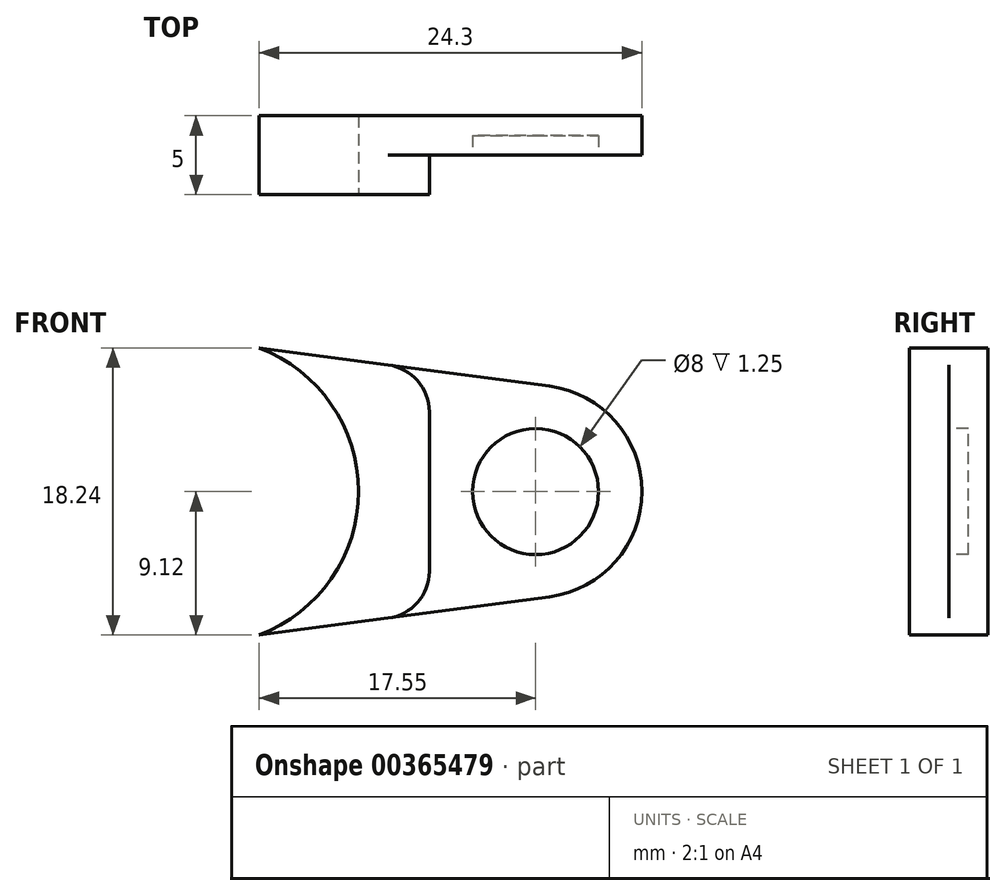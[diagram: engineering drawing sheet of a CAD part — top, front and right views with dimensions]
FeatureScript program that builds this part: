
annotation { "Feature Type Name" : "Feature", "Feature Type Description" : "" }
export const myFeature = defineFeature(function(context is Context, id is Id, definition is map)
    precondition{}
    {
        {
            var Q0;
            Q0=qCreatedBy(makeId("Front.planeOp"),FACE);
            var sketch = newSketch(context, id + "F0", { "sketchPlane" : qUnion([Q0])});
            skCircle(sketch, "E0", {"center": v(0, 0) * mm, "radius": 8 * mm});
            skCircle(sketch, "E1", {"center": v(0, 0) * mm, "radius": 9.5 * mm});
            skLineSegment(sketch, "E2", {"start": v(0, 0) * mm, "end": v(0, -1.5) * mm});
            skLineSegment(sketch, "E3", {"start": v(0, 0) * mm, "end": v(0, 1.5) * mm});
            skLineSegment(sketch, "E4", {"start": v(-32.5, 0) * mm, "end": v(-32.5, 1.5) * mm});
            skLineSegment(sketch, "E5", {"start": v(-32.5, 0) * mm, "end": v(-32.5, -1.5) * mm});
            skLineSegment(sketch, "E6", {"start": v(-32.5, -1.5) * mm, "end": v(-32.5, -2.5) * mm});
            skLineSegment(sketch, "E7", {"start": v(-23.5, -8) * mm, "end": v(-5.12, -8) * mm});
            skLineSegment(sketch, "E8.MirrorCS", {"start": v(-32.5, 1.5) * mm, "end": v(-32.5, 3.5) * mm});
            skLineSegment(sketch, "E9", {"start": v(-25.5, 0) * mm, "end": v(-25.5, -6) * mm});
            skLineSegment(sketch, "E10", {"start": v(-32.5, 1.5) * mm, "end": v(-32.5, 2.5) * mm});
            skLineSegment(sketch, "E11", {"start": v(-32.5, -1.5) * mm, "end": v(-32.5, -3.5) * mm});
            skLineSegment(sketch, "E12", {"start": v(-31.5, -3.5) * mm, "end": v(-25.5, -3.5) * mm});
            skLineSegment(sketch, "E13", {"start": v(-31.5, 3.5) * mm, "end": v(-25.5, 3.5) * mm});
            skPoint(sketch, "E14.orphan", {"position": v(-32.5, 8) * mm});
            skPoint(sketch, "E15.orphan", {"position": v(-32.5, -8) * mm});
            skPoint(sketch, "E16.visualSharp", {"position": v(-25.5, 8) * mm});
            skPoint(sketch, "E17.visualSharp", {"position": v(-25.5, -8) * mm});
            skArc(sketch, "E17.filletArc", {"start": v(-25.5, -6) * mm, "mid": v(-24.91, -7.41) * mm, "end": v(-23.5, -8) * mm});
            skPoint(sketch, "E18.visualSharp", {"position": v(-32.5, 3.5) * mm});
            skArc(sketch, "E18.filletArc", {"start": v(-31.5, 3.5) * mm, "mid": v(-32.2, 3.2) * mm, "end": v(-32.5, 2.5) * mm});
            skPoint(sketch, "E19.visualSharp", {"position": v(-32.5, -3.5) * mm});
            skArc(sketch, "E19.filletArc", {"start": v(-32.5, -2.5) * mm, "mid": v(-32.2, -3.2) * mm, "end": v(-31.5, -3.5) * mm});
            skPoint(sketch, "E20.orphan", {"position": v(-2.5, 8) * mm});
            skPoint(sketch, "E21.orphan", {"position": v(-2.5, -8) * mm});
            skLineSegment(sketch, "E22", {"start": v(-25.5, 3.5) * mm, "end": v(-8.83, 3.5) * mm});
            skLineSegment(sketch, "E23", {"start": v(-25.5, -3.5) * mm, "end": v(-25.5, 3) * mm});
            skLineSegment(sketch, "E24", {"start": v(-23.5, 5) * mm, "end": v(-8.08, 5) * mm});
            skPoint(sketch, "E25.visualSharp", {"position": v(-25.5, 5) * mm});
            skArc(sketch, "E25.filletArc", {"start": v(-23.5, 5) * mm, "mid": v(-24.91, 4.41) * mm, "end": v(-25.5, 3) * mm});
            skSolve(sketch);
        }
        {
            var Q0;
            Q0=qSketchRegion(id+"F0",true);
            extrude(context, id + "F1", {"entities" : qUnion([Q0]), "depth" : 10 * mm});
        }
        {
            var Q0;
            Q0=makeQuery(id+"F1.opExtrude","SWEPT_FACE",FACE,{"disambiguationData":[OSD([sQuery(id+"F0.wireOp",EDGE,"E4"),sQuery(id+"F0.wireOp",EDGE,"E5"),sQuery(id+"F0.wireOp",EDGE,"E10"),sQuery(id+"F0.wireOp",EDGE,"E11")])]});
            var sketch = newSketch(context, id + "F2", { "sketchPlane" : qUnion([Q0])});
            skCircle(sketch, "E26", {"center": v(5, 0) * mm, "radius": 1.5 * mm});
            skPoint(sketch, "E26.centerSnap1", {"position": v(5, -2.5) * mm});
            skSolve(sketch);
        }
        {
            var Q0;
            Q0=qSketchRegion(id+"F2",true);
            extrude(context, id + "F3", {"entities" : qUnion([Q0]), "operationType" : NewBodyOperationType.REMOVE, "oppositeDirection" : true, "depth" : 22.1 * mm});
        }
        {
            var Q0;
            Q0=makeQuery(id+"F1.opExtrude","SWEPT_FACE",FACE,{"disambiguationData":[OSD([sQuery(id+"F0.wireOp",EDGE,"E7")])]});
            var sketch = newSketch(context, id + "F4", { "sketchPlane" : qUnion([Q0])});
            skLineSegment(sketch, "E27", {"start": v(-11, 5) * mm, "end": v(-12.4, 5) * mm});
            skCircle(sketch, "E28", {"center": v(-12.4, 5) * mm, "radius": 1.4 * mm});
            skLineSegment(sketch, "E29", {"start": v(-23.5, 5) * mm, "end": v(-22.5, 5) * mm});
            skCircle(sketch, "E30", {"center": v(-19.5, 5) * mm, "radius": 1.4 * mm});
            skSolve(sketch);
        }
        {
            var Q0;
            Q0=qSketchRegion(id+"F4",true);
            extrude(context, id + "F5", {"entities" : qUnion([Q0]), "operationType" : NewBodyOperationType.REMOVE, "oppositeDirection" : true, "depth" : 8 * mm});
        }
        {
            var Q0;
            Q0=makeQuery(id+"F1.opExtrude","CAP_EDGE",EDGE,{"disambiguationData":[OSD([sQuery(id+"F0.wireOp",EDGE,"E24")])],"isStart":false});
            var Q1;
            Q1=makeQuery(id+"F1.opExtrude","CAP_EDGE",EDGE,{"disambiguationData":[OSD([sQuery(id+"F0.wireOp",EDGE,"E24")])],"isStart":true});
            fillet(context, id + "F6", {"entities" : qUnion([Q0, Q1]), "radius" : 2 * mm, "tangentPropagation" : true, "allowEdgeOverflow" : false});
        }
        {
            var Q0;
            Q0=makeQuery(id+"F1.opExtrude","CAP_EDGE",EDGE,{"disambiguationData":[OSD([sQuery(id+"F0.wireOp",EDGE,"E4"),sQuery(id+"F0.wireOp",EDGE,"E5"),sQuery(id+"F0.wireOp",EDGE,"E10"),sQuery(id+"F0.wireOp",EDGE,"E11")])],"isStart":false});
            var Q1;
            Q1=makeQuery(id+"F1.opExtrude","CAP_EDGE",EDGE,{"disambiguationData":[OSD([sQuery(id+"F0.wireOp",EDGE,"E4"),sQuery(id+"F0.wireOp",EDGE,"E5"),sQuery(id+"F0.wireOp",EDGE,"E10"),sQuery(id+"F0.wireOp",EDGE,"E11")])],"isStart":true});
            fillet(context, id + "F7", {"entities" : qUnion([Q0, Q1]), "radius" : 2 * mm, "tangentPropagation" : true, "allowEdgeOverflow" : false});
        }
        {
            var Q0;
            Q0=makeQuery(id+"F1.opExtrude","CAP_EDGE",EDGE,{"disambiguationData":[OSD([sQuery(id+"F0.wireOp",EDGE,"E7")])],"isStart":false});
            var Q1;
            Q1=makeQuery(id+"F1.opExtrude","CAP_EDGE",EDGE,{"disambiguationData":[OSD([sQuery(id+"F0.wireOp",EDGE,"E7")])],"isStart":true});
            fillet(context, id + "F8", {"entities" : qUnion([Q0, Q1]), "radius" : 2 * mm, "tangentPropagation" : true, "allowEdgeOverflow" : false});
        }
        {
            var Q0;
            Q0=qCreatedBy(makeId("Front.planeOp"),FACE);
            var sketch = newSketch(context, id + "F9", { "sketchPlane" : qUnion([Q0])});
            skLineSegment(sketch, "E31", {"start": v(8.71, 0) * mm, "end": v(21, 0) * mm});
            skCircle(sketch, "E32", {"center": v(21, 0) * mm, "radius": 6.75 * mm});
            skLineSegment(sketch, "E33", {"start": v(21, 0) * mm, "end": v(21, -5.45) * mm});
            skLineSegment(sketch, "E34", {"start": v(21, 0) * mm, "end": v(21.88, -6.7) * mm});
            skLineSegment(sketch, "E35", {"start": v(21.88, -6.7) * mm, "end": v(0.83, -9.46) * mm});
            skArc(sketch, "E36", {"start": v(0.83, -9.46) * mm, "mid": v(1.24, -9.42) * mm, "end": v(1.65, -9.36) * mm});
            skArc(sketch, "E37.MirrorCS", {"start": v(0.83, 9.46) * mm, "mid": v(1.24, 9.42) * mm, "end": v(1.65, 9.36) * mm});
            skLineSegment(sketch, "E38.MirrorCS", {"start": v(21.88, 6.7) * mm, "end": v(0.83, 9.46) * mm});
            skArc(sketch, "E39", {"start": v(0.83, -8.67) * mm, "mid": v(8.71, 0) * mm, "end": v(0.83, 8.67) * mm});
            skLineSegment(sketch, "E40", {"start": v(0.83, 9.46) * mm, "end": v(0.83, 8.67) * mm});
            skPoint(sketch, "E41.orphan", {"position": v(9.5, 0) * mm});
            skLineSegment(sketch, "E42.trimOffspring", {"start": v(0.83, -8.67) * mm, "end": v(0.83, -9.46) * mm});
            skSolve(sketch);
        }
        {
            var Q0;
            Q0=qSketchRegion(id+"F9",true);
            extrude(context, id + "F10", {"entities" : qUnion([Q0]), "operationType" : NewBodyOperationType.ADD, "depth" : 2.5 * mm});
        }
        {
            var Q0;
            Q0=makeQuery(id+"F10.opExtrude","CAP_FACE",FACE,{"disambiguationData":[OSD([sQuery(id+"F9.wireOp",EDGE,"E32"),sQuery(id+"F9.wireOp",EDGE,"E35"),sQuery(id+"F9.wireOp",EDGE,"E36"),sQuery(id+"F9.wireOp",EDGE,"E37.MirrorCS"),sQuery(id+"F9.wireOp",EDGE,"E38.MirrorCS"),sQuery(id+"F9.wireOp",EDGE,"E39"),sQuery(id+"F9.wireOp",EDGE,"E40"),sQuery(id+"F9.wireOp",EDGE,"E42.trimOffspring")])],"isStart":false});
            var sketch = newSketch(context, id + "F11", { "sketchPlane" : qUnion([Q0])});
            skCircle(sketch, "E43", {"center": v(21, 0) * mm, "radius": 4 * mm});
            skSolve(sketch);
        }
        {
            var Q0;
            Q0=qSketchRegion(id+"F11",true);
            extrude(context, id + "F12", {"entities" : qUnion([Q0]), "operationType" : NewBodyOperationType.ADD, "depth" : 6 * mm});
        }
        {
            var Q0;
            Q0=makeQuery(id+"F10.opExtrude","CAP_FACE",FACE,{"disambiguationData":[OSD([sQuery(id+"F9.wireOp",EDGE,"E32"),sQuery(id+"F9.wireOp",EDGE,"E35"),sQuery(id+"F9.wireOp",EDGE,"E36"),sQuery(id+"F9.wireOp",EDGE,"E37.MirrorCS"),sQuery(id+"F9.wireOp",EDGE,"E38.MirrorCS"),sQuery(id+"F9.wireOp",EDGE,"E39"),sQuery(id+"F9.wireOp",EDGE,"E40"),sQuery(id+"F9.wireOp",EDGE,"E42.trimOffspring")])],"isStart":false});
            var sketch = newSketch(context, id + "F13", { "sketchPlane" : qUnion([Q0])});
            skLineSegment(sketch, "E44", {"start": v(14.25, 0) * mm, "end": v(14.25, 7.7) * mm});
            skLineSegment(sketch, "E45", {"start": v(1.65, 9.36) * mm, "end": v(14.25, 7.7) * mm});
            skArc(sketch, "E46", {"start": v(1.65, -8.34) * mm, "mid": v(8.5, 0) * mm, "end": v(1.65, 8.34) * mm});
            skLineSegment(sketch, "E47", {"start": v(1.65, 9.36) * mm, "end": v(1.65, 8.34) * mm});
            skLineSegment(sketch, "E48.MirrorCS", {"start": v(1.65, -9.36) * mm, "end": v(1.65, -8.34) * mm});
            skLineSegment(sketch, "E49.MirrorCS", {"start": v(1.65, -9.36) * mm, "end": v(14.25, -7.7) * mm});
            skLineSegment(sketch, "E50.MirrorCS", {"start": v(14.25, 0) * mm, "end": v(14.25, -7.7) * mm});
            skPoint(sketch, "E51.start.orphan", {"position": v(9.5, 0) * mm});
            skSolve(sketch);
        }
        {
            var Q0;
            Q0=qSketchRegion(id+"F13",true);
            extrude(context, id + "F14", {"entities" : qUnion([Q0]), "operationType" : NewBodyOperationType.ADD, "depth" : 2.5 * mm});
        }
        {
            var Q0;
            Q0=makeQuery(id+"F14.opExtrude","SWEPT_EDGE",EDGE,{"disambiguationData":[OSD([sQuery(id+"F9.wireOp",EDGE,"E38.MirrorCS"),sQuery(id+"F13.wireOp",EDGE,"E44"),sQuery(id+"F13.wireOp",EDGE,"E45")])]});
            var Q1;
            Q1=makeQuery(id+"F14.opExtrude","SWEPT_EDGE",EDGE,{"disambiguationData":[OSD([sQuery(id+"F9.wireOp",EDGE,"E35"),sQuery(id+"F13.wireOp",EDGE,"E49.MirrorCS"),sQuery(id+"F13.wireOp",EDGE,"E50.MirrorCS")])]});
            fillet(context, id + "F15", {"entities" : qUnion([Q0, Q1]), "radius" : 3 * mm, "tangentPropagation" : true, "allowEdgeOverflow" : false});
        }
        {
            var Q0;
            Q0=makeQuery(id+"F1.opExtrude","CAP_FACE",FACE,{"disambiguationData":[OSD([sQuery(id+"F0.wireOp",EDGE,"E0"),sQuery(id+"F0.wireOp",EDGE,"E1"),sQuery(id+"F0.wireOp",EDGE,"E4"),sQuery(id+"F0.wireOp",EDGE,"E5"),sQuery(id+"F0.wireOp",EDGE,"E7"),sQuery(id+"F0.wireOp",EDGE,"E9"),sQuery(id+"F0.wireOp",EDGE,"E10"),sQuery(id+"F0.wireOp",EDGE,"E11"),sQuery(id+"F0.wireOp",EDGE,"E12"),sQuery(id+"F0.wireOp",EDGE,"E13"),sQuery(id+"F0.wireOp",EDGE,"E17.filletArc"),sQuery(id+"F0.wireOp",EDGE,"E18.filletArc"),sQuery(id+"F0.wireOp",EDGE,"E19.filletArc"),sQuery(id+"F0.wireOp",EDGE,"E22"),sQuery(id+"F0.wireOp",EDGE,"E24"),sQuery(id+"F0.wireOp",EDGE,"E25.filletArc")])],"isStart":false});
            var sketch = newSketch(context, id + "F16", { "sketchPlane" : qUnion([Q0])});
            skArc(sketch, "E52", {"start": v(0, -9.75) * mm, "mid": v(9.75, 0) * mm, "end": v(0, 9.75) * mm});
            skLineSegment(sketch, "E53", {"start": v(0, 9.75) * mm, "end": v(0, 13.42) * mm});
            skLineSegment(sketch, "E54", {"start": v(0, 13.42) * mm, "end": v(-34.7, 13.42) * mm});
            skLineSegment(sketch, "E55", {"start": v(0, -9.75) * mm, "end": v(-37.45, -9.75) * mm});
            skLineSegment(sketch, "E56", {"start": v(-37.45, -9.75) * mm, "end": v(-37.45, 13.42) * mm});
            skLineSegment(sketch, "E57", {"start": v(-37.45, 13.42) * mm, "end": v(-34.7, 13.42) * mm});
            skSolve(sketch);
        }
        {
            var Q0;
            Q0 = qSketchRegion(id + "F16", true);
            extrude(context, id + "F17", {"entities" : qUnion([Q0]), "operationType" : NewBodyOperationType.REMOVE, "oppositeDirection" : true, "depth" : 25 * mm});
        }
        {
            var Q0;
            Q0=makeQuery(id+"F12.opExtrude","CAP_FACE",FACE,{"disambiguationData":[OSD([sQuery(id+"F11.wireOp",EDGE,"E43")])],"isStart":false});
            extrude(context, id + "F18", {"entities" : qUnion([Q0]), "operationType" : NewBodyOperationType.REMOVE, "oppositeDirection" : true, "depth" : 7.25 * mm});
        }
    });
